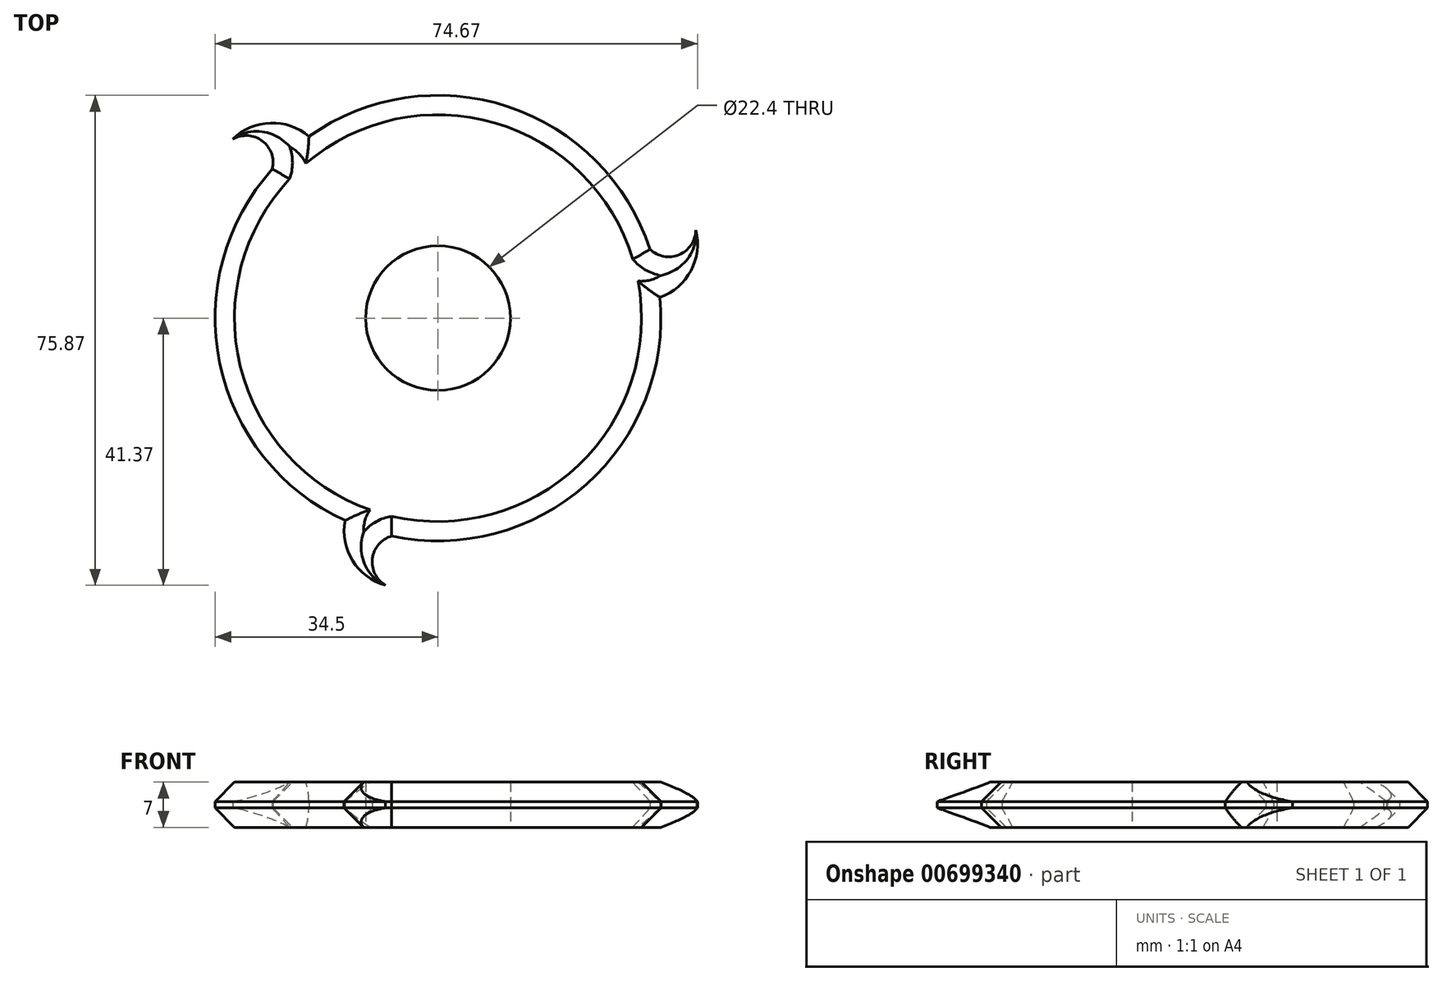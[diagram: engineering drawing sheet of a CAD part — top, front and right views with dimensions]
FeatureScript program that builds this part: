
annotation { "Feature Type Name" : "Feature", "Feature Type Description" : "" }
export const myFeature = defineFeature(function(context is Context, id is Id, definition is map)
    precondition{}
    {
        {
            var Q0;
            Q0=qCreatedBy(makeId("Top.planeOp"),FACE);
            var sketch = newSketch(context, id + "F0", { "sketchPlane" : qUnion([Q0])});
            skCircle(sketch, "E0", {"center": v(0, 0) * mm, "radius": 11.2 * mm});
            skArc(sketch, "E1", {"start": v(-25.64, 23.08) * mm, "mid": v(-33.78, -6.99) * mm, "end": v(-14.38, -31.36) * mm});
            skArc(sketch, "E2", {"start": v(-19.97, 28.13) * mm, "mid": v(-25.94, 30.22) * mm, "end": v(-31.76, 27.73) * mm});
            skArc(sketch, "E3", {"start": v(-25.64, 23.08) * mm, "mid": v(-27.17, 27.42) * mm, "end": v(-31.76, 27.73) * mm});
            skArc(sketch, "E4.1.0", {"start": v(-14.38, -31.36) * mm, "mid": v(-13.2, -37.57) * mm, "end": v(-8.14, -41.37) * mm});
            skArc(sketch, "E4.1.1", {"start": v(-7.17, -33.75) * mm, "mid": v(-10.16, -37.24) * mm, "end": v(-8.14, -41.37) * mm});
            skArc(sketch, "E4.2.0", {"start": v(34.35, 3.22) * mm, "mid": v(39.14, 7.36) * mm, "end": v(39.9, 13.64) * mm});
            skArc(sketch, "E4.2.1", {"start": v(32.8, 10.67) * mm, "mid": v(37.33, 9.82) * mm, "end": v(39.9, 13.64) * mm});
            skArc(sketch, "E5.trimOffspring", {"start": v(32.8, 10.67) * mm, "mid": v(10.84, 32.75) * mm, "end": v(-19.97, 28.13) * mm});
            skArc(sketch, "E6.trimOffspring", {"start": v(-7.17, -33.75) * mm, "mid": v(22.94, -25.76) * mm, "end": v(34.35, 3.22) * mm});
            skSolve(sketch);
        }
        {
            var Q0;
            Q0=makeQuery(id+"F0.imprint","IMPRINT",FACE,{"disambiguationData":[TD([[makeQuery(id+"F0.imprint","IMPRINT",EDGE,{"derivedFrom":sQuery(id+"F0.wireOp",EDGE,"E0")}),-1.0]])]});
            extrude(context, id + "F1", {"entities" : qUnion([Q0]), "depth" : 7 * mm, "offsetDistance" : 25 * mm});
        }
        {
            var Q0;
            Q0=makeQuery(id+"F1.opExtrude","CAP_EDGE",EDGE,{"disambiguationData":[OSD([sQuery(id+"F0.wireOp",EDGE,"E5.trimOffspring")])],"isStart":false});
            var Q1;
            Q1=makeQuery(id+"F1.opExtrude","CAP_EDGE",EDGE,{"disambiguationData":[OSD([sQuery(id+"F0.wireOp",EDGE,"E2")])],"isStart":false});
            var Q2;
            Q2=makeQuery(id+"F1.opExtrude","CAP_EDGE",EDGE,{"disambiguationData":[OSD([sQuery(id+"F0.wireOp",EDGE,"E1")])],"isStart":false});
            var Q3;
            Q3=makeQuery(id+"F1.opExtrude","CAP_EDGE",EDGE,{"disambiguationData":[OSD([sQuery(id+"F0.wireOp",EDGE,"E3")])],"isStart":false});
            var Q4;
            Q4=makeQuery(id+"F1.opExtrude","CAP_EDGE",EDGE,{"disambiguationData":[OSD([sQuery(id+"F0.wireOp",EDGE,"E4.1.0")])],"isStart":false});
            var Q5;
            Q5=makeQuery(id+"F1.opExtrude","CAP_EDGE",EDGE,{"disambiguationData":[OSD([sQuery(id+"F0.wireOp",EDGE,"E4.1.1")])],"isStart":false});
            var Q6;
            Q6=makeQuery(id+"F1.opExtrude","CAP_EDGE",EDGE,{"disambiguationData":[OSD([sQuery(id+"F0.wireOp",EDGE,"E6.trimOffspring")])],"isStart":false});
            var Q7;
            Q7=makeQuery(id+"F1.opExtrude","CAP_EDGE",EDGE,{"disambiguationData":[OSD([sQuery(id+"F0.wireOp",EDGE,"E4.2.0")])],"isStart":false});
            var Q8;
            Q8=makeQuery(id+"F1.opExtrude","CAP_EDGE",EDGE,{"disambiguationData":[OSD([sQuery(id+"F0.wireOp",EDGE,"E4.2.1")])],"isStart":false});
            var Q9;
            Q9=makeQuery(id+"F1.opExtrude","CAP_EDGE",EDGE,{"disambiguationData":[OSD([sQuery(id+"F0.wireOp",EDGE,"E6.trimOffspring")])],"isStart":true});
            var Q10;
            Q10=makeQuery(id+"F1.opExtrude","CAP_EDGE",EDGE,{"disambiguationData":[OSD([sQuery(id+"F0.wireOp",EDGE,"E5.trimOffspring")])],"isStart":true});
            var Q11;
            Q11=makeQuery(id+"F1.opExtrude","CAP_EDGE",EDGE,{"disambiguationData":[OSD([sQuery(id+"F0.wireOp",EDGE,"E1")])],"isStart":true});
            var Q12;
            Q12=makeQuery(id+"F1.opExtrude","CAP_EDGE",EDGE,{"disambiguationData":[OSD([sQuery(id+"F0.wireOp",EDGE,"E4.1.1")])],"isStart":true});
            var Q13;
            Q13=makeQuery(id+"F1.opExtrude","CAP_EDGE",EDGE,{"disambiguationData":[OSD([sQuery(id+"F0.wireOp",EDGE,"E4.1.0")])],"isStart":true});
            var Q14;
            Q14=makeQuery(id+"F1.opExtrude","CAP_EDGE",EDGE,{"disambiguationData":[OSD([sQuery(id+"F0.wireOp",EDGE,"E4.2.0")])],"isStart":true});
            var Q15;
            Q15=makeQuery(id+"F1.opExtrude","CAP_EDGE",EDGE,{"disambiguationData":[OSD([sQuery(id+"F0.wireOp",EDGE,"E4.2.1")])],"isStart":true});
            var Q16;
            Q16=makeQuery(id+"F1.opExtrude","CAP_EDGE",EDGE,{"disambiguationData":[OSD([sQuery(id+"F0.wireOp",EDGE,"E2")])],"isStart":true});
            var Q17;
            Q17=makeQuery(id+"F1.opExtrude","CAP_EDGE",EDGE,{"disambiguationData":[OSD([sQuery(id+"F0.wireOp",EDGE,"E3")])],"isStart":true});
            chamfer(context, id + "F2", {"entities" : qUnion([Q0, Q1, Q2, Q3, Q4, Q5, Q6, Q7, Q8, Q9, Q10, Q11, Q12, Q13, Q14, Q15, Q16, Q17]), "width" : 3 * mm, "tangentPropagation" : true});
        }
    });
